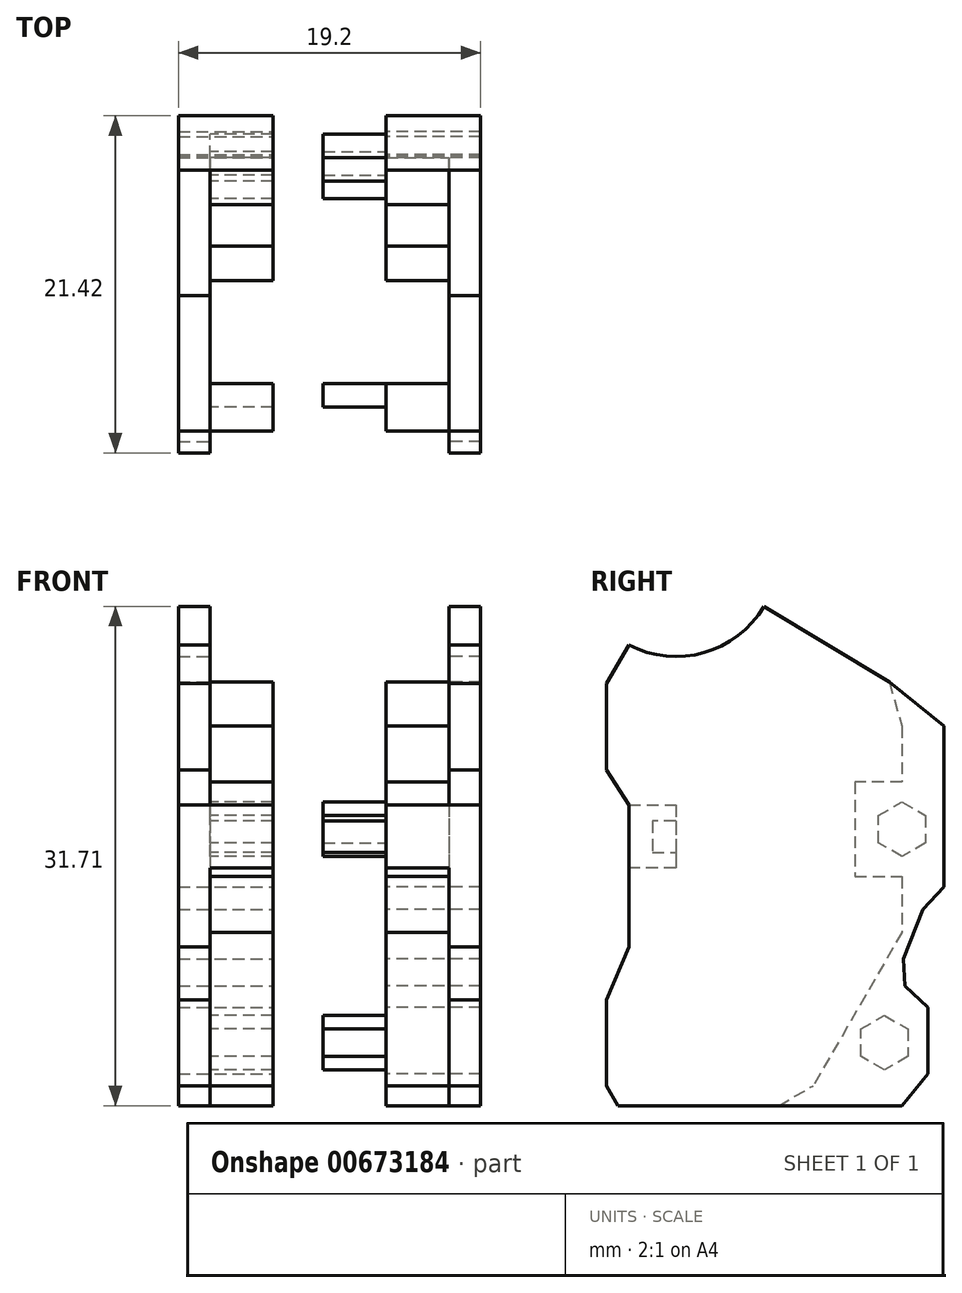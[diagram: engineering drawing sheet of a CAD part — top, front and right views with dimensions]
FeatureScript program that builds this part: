
annotation { "Feature Type Name" : "Feature", "Feature Type Description" : "" }
export const myFeature = defineFeature(function(context is Context, id is Id, definition is map)
    precondition{}
    {
        {
            var Q0;
            Q0=qCreatedBy(makeId("Right.planeOp"),FACE);
            cPlane(context, id + "F0", {"entities" : qUnion([Q0]), "cplaneType" : CPlaneType.OFFSET, "offset" : 7.6 * mm, "width" : 150 * mm, "height" : 150 * mm});
        }
        {
            var Q0;
            Q0=qCreatedBy(makeId("Right.planeOp"),FACE);
            var sketch = newSketch(context, id + "F1", { "sketchPlane" : qUnion([Q0])});
            skLineSegment(sketch, "E0.4", {"start": v(1.48, 13.79) * mm, "end": v(1.48, 12.29) * mm, "construction": true});
            skLineSegment(sketch, "E0.12", {"start": v(1.48, 9.69) * mm, "end": v(1.48, 2.79) * mm, "construction": true});
            skLineSegment(sketch, "E1.MirrorCS", {"start": v(-0.77, 10.55) * mm, "end": v(-0.77, 9.69) * mm, "construction": true});
            skLineSegment(sketch, "E2.MirrorCS", {"start": v(-0.02, 10.99) * mm, "end": v(-0.77, 10.55) * mm, "construction": true});
            skLineSegment(sketch, "E3.MirrorCS", {"start": v(-0.02, 12.29) * mm, "end": v(-0.02, 10.99) * mm, "construction": true});
            skLineSegment(sketch, "E4.MirrorCS", {"start": v(1.48, 12.29) * mm, "end": v(-0.02, 12.29) * mm, "construction": true});
            skArc(sketch, "E5.MirrorCS", {"start": v(0.48, 14.79) * mm, "mid": v(1.18, 14.5) * mm, "end": v(1.48, 13.79) * mm, "construction": true});
            skLineSegment(sketch, "E6.MirrorCS", {"start": v(-6.02, 8.55) * mm, "end": v(-6.02, 9.69) * mm, "construction": true});
            skLineSegment(sketch, "E7.MirrorCS", {"start": v(-4.52, 12.29) * mm, "end": v(-6.02, 12.29) * mm, "construction": true});
            skLineSegment(sketch, "E8.MirrorCS", {"start": v(-4.52, 10.99) * mm, "end": v(-4.52, 12.29) * mm, "construction": true});
            skLineSegment(sketch, "E9.MirrorCS", {"start": v(-3.77, 9.69) * mm, "end": v(-3.77, 10.55) * mm, "construction": true});
            skLineSegment(sketch, "E10.MirrorCS", {"start": v(-3.77, 10.55) * mm, "end": v(-4.52, 10.99) * mm, "construction": true});
            skLineSegment(sketch, "E11.MirrorCS", {"start": v(-0.77, 9.69) * mm, "end": v(1.48, 9.69) * mm, "construction": true});
            skLineSegment(sketch, "E12.MirrorCS", {"start": v(-5.02, 14.79) * mm, "end": v(0.48, 14.79) * mm, "construction": true});
            skArc(sketch, "E13.MirrorCS", {"start": v(-6.02, 13.79) * mm, "mid": v(-5.73, 14.5) * mm, "end": v(-5.02, 14.79) * mm, "construction": true});
            skLineSegment(sketch, "E14.MirrorCS", {"start": v(-5.02, 6.82) * mm, "end": v(-6.02, 8.55) * mm, "construction": true});
            skArc(sketch, "E15.MirrorCS", {"start": v(1.48, 2.79) * mm, "mid": v(-5.4, -1.04) * mm, "end": v(-5.02, 6.82) * mm, "construction": true});
            skLineSegment(sketch, "E16.MirrorCS", {"start": v(-6.02, 12.29) * mm, "end": v(-6.02, 13.79) * mm, "construction": true});
            skLineSegment(sketch, "E17.MirrorCS", {"start": v(-6.02, 9.69) * mm, "end": v(-3.77, 9.69) * mm, "construction": true});
            skLineSegment(sketch, "E18", {"start": v(-6.02, 8.55) * mm, "end": v(-7.43, 10.99) * mm, "construction": true});
            skLineSegment(sketch, "E19", {"start": v(-7.43, 10.99) * mm, "end": v(-11.18, 10.99) * mm, "construction": true});
            skLineSegment(sketch, "E20", {"start": v(-7.43, 10.99) * mm, "end": v(-10.15, 12.25) * mm, "construction": true});
            skLineSegment(sketch, "E21", {"start": v(-10.15, 12.25) * mm, "end": v(-10.15, 16.25) * mm, "construction": true});
            skLineSegment(sketch, "E22", {"start": v(-10.15, 14.25) * mm, "end": v(-8.02, 14.25) * mm, "construction": true});
            skLineSegment(sketch, "E23", {"start": v(-10.15, 16.25) * mm, "end": v(-7.15, 21.25) * mm, "construction": true});
            skLineSegment(sketch, "E24", {"start": v(-7.15, 21.25) * mm, "end": v(4.13, 21.25) * mm, "construction": true});
            skLineSegment(sketch, "E25", {"start": v(4.13, 21.25) * mm, "end": v(7.28, 16.25) * mm, "construction": true});
            skLineSegment(sketch, "E26", {"start": v(7.28, 16.25) * mm, "end": v(7.28, 9.57) * mm, "construction": true});
            skLineSegment(sketch, "E27", {"start": v(7.28, 9.57) * mm, "end": v(1.48, 6.24) * mm, "construction": true});
            skLineSegment(sketch, "E28", {"start": v(1.48, 6.24) * mm, "end": v(1.48, 9.69) * mm, "construction": true});
            skArc(sketch, "E29", {"start": v(0.22, 5.9) * mm, "mid": v(-2.25, 7.22) * mm, "end": v(-5.02, 6.82) * mm, "construction": true});
            skLineSegment(sketch, "E30", {"start": v(1.48, 6.24) * mm, "end": v(0.22, 5.9) * mm, "construction": true});
            skCircle(sketch, "E31", {"center": v(-3.02, 2.79) * mm, "radius": 4.5 * mm});
            skCircle(sketch, "E32", {"center": v(-3.02, 2.79) * mm, "radius": 3.5 * mm});
            skLineSegment(sketch, "E33", {"start": v(-3.02, 2.79) * mm, "end": v(-7.52, 2.79) * mm, "construction": true});
            skPoint(sketch, "E34.MirrorCS.end.orphan", {"position": v(-7.43, -5.42) * mm});
            skPoint(sketch, "E34.MirrorCS.start.orphan", {"position": v(-6.02, -2.98) * mm});
            skPoint(sketch, "E35.MirrorCS.start.orphan", {"position": v(-5.02, -1.25) * mm});
            skLineSegment(sketch, "E36", {"start": v(-5.02, -1.25) * mm, "end": v(-7.43, -5.42) * mm});
            skLineSegment(sketch, "E37", {"start": v(-6.02, -2.98) * mm, "end": v(-6.02, -30.98) * mm, "construction": true});
            skLineSegment(sketch, "E38", {"start": v(-7.43, -5.42) * mm, "end": v(-7.43, -10.9) * mm});
            skLineSegment(sketch, "E39", {"start": v(-7.43, -10.9) * mm, "end": v(-6.02, -13.15) * mm});
            skLineSegment(sketch, "E40", {"start": v(-6.02, -13.15) * mm, "end": v(-6.02, -22.15) * mm});
            skLineSegment(sketch, "E41", {"start": v(-6.02, -22.15) * mm, "end": v(-7.43, -25.53) * mm});
            skLineSegment(sketch, "E42", {"start": v(-7.43, -25.53) * mm, "end": v(-7.43, -30.98) * mm});
            skLineSegment(sketch, "E43", {"start": v(-7.43, -30.98) * mm, "end": v(-6.02, -33.4) * mm});
            skLineSegment(sketch, "E44", {"start": v(-6.02, -33.4) * mm, "end": v(1.48, -33.4) * mm});
            skLineSegment(sketch, "E45", {"start": v(1.48, -33.4) * mm, "end": v(1.48, 2.79) * mm, "construction": true});
            skLineSegment(sketch, "E46", {"start": v(1.48, -33.4) * mm, "end": v(5.7, -30.98) * mm});
            skLineSegment(sketch, "E47", {"start": v(1.48, 0.12) * mm, "end": v(1.48, 2.79) * mm});
            skLineSegment(sketch, "E48", {"start": v(10.53, -5.34) * mm, "end": v(11.33, -8.13) * mm});
            skLineSegment(sketch, "E49", {"start": v(11.33, -8.13) * mm, "end": v(11.33, -11.68) * mm});
            skLineSegment(sketch, "E50", {"start": v(11.33, -21.24) * mm, "end": v(5.7, -30.98) * mm});
            skPoint(sketch, "E51.end.orphan", {"position": v(7.28, -24.1) * mm});
            skPoint(sketch, "E52.orphan", {"position": v(9.73, -2.54) * mm});
            skPoint(sketch, "E53.orphan", {"position": v(1.48, -2.54) * mm});
            skPoint(sketch, "E54.start.orphan", {"position": v(5.6, -2.54) * mm});
            skLineSegment(sketch, "E55", {"start": v(1.48, 0.12) * mm, "end": v(1.91, -0.14) * mm});
            skLineSegment(sketch, "E56", {"start": v(11.33, -11.68) * mm, "end": v(8.33, -11.68) * mm});
            skLineSegment(sketch, "E57", {"start": v(8.33, -11.68) * mm, "end": v(8.33, -17.68) * mm});
            skLineSegment(sketch, "E58", {"start": v(8.33, -17.68) * mm, "end": v(11.33, -17.68) * mm});
            skLineSegment(sketch, "E59.trimOffspring", {"start": v(11.33, -17.68) * mm, "end": v(11.33, -21.24) * mm});
            skPoint(sketch, "E60.start.orphan", {"position": v(11.33, -14.68) * mm});
            skLineSegment(sketch, "E61", {"start": v(1.91, -0.14) * mm, "end": v(2.86, 2.73) * mm});
            skLineSegment(sketch, "E62", {"start": v(2.86, 2.73) * mm, "end": v(2.86, 5.9) * mm});
            skLineSegment(sketch, "E63", {"start": v(2.86, 5.9) * mm, "end": v(8.23, 9.33) * mm});
            skLineSegment(sketch, "E64", {"start": v(8.23, 9.33) * mm, "end": v(8.71, 10.78) * mm});
            skLineSegment(sketch, "E65", {"start": v(8.71, 10.78) * mm, "end": v(10.24, 10.27) * mm});
            skLineSegment(sketch, "E66", {"start": v(10.24, 10.27) * mm, "end": v(12.91, 5.96) * mm});
            skLineSegment(sketch, "E67", {"start": v(12.91, 5.96) * mm, "end": v(12.91, 0.6) * mm});
            skLineSegment(sketch, "E68", {"start": v(12.91, 0.6) * mm, "end": v(10.53, -5.34) * mm});
            skLineSegment(sketch, "E69", {"start": v(10.53, -5.34) * mm, "end": v(1.91, -0.14) * mm});
            skArc(sketch, "E70", {"start": v(-6.02, -2.98) * mm, "mid": v(-1.25, -3.46) * mm, "end": v(2.56, -0.53) * mm});
            skLineSegment(sketch, "E71", {"start": v(10.53, -5.34) * mm, "end": v(14, -8.13) * mm});
            skLineSegment(sketch, "E72", {"start": v(14, -8.13) * mm, "end": v(14, -18.34) * mm});
            skLineSegment(sketch, "E73", {"start": v(14, -18.34) * mm, "end": v(12.66, -19.79) * mm});
            skCircle(sketch, "E74.cCircle", {"center": v(11.33, -14.68) * mm, "radius": 1.5 * mm, "construction": true});
            skLineSegment(sketch, "E74.0", {"start": v(9.83, -15.55) * mm, "end": v(9.83, -13.82) * mm});
            skLineSegment(sketch, "E74.1", {"start": v(9.83, -13.82) * mm, "end": v(11.33, -12.95) * mm});
            skLineSegment(sketch, "E74.2", {"start": v(11.33, -12.95) * mm, "end": v(12.83, -13.82) * mm});
            skLineSegment(sketch, "E74.3", {"start": v(12.83, -13.82) * mm, "end": v(12.83, -15.55) * mm});
            skLineSegment(sketch, "E74.4", {"start": v(12.83, -15.55) * mm, "end": v(11.33, -16.41) * mm});
            skLineSegment(sketch, "E74.5", {"start": v(11.33, -16.41) * mm, "end": v(9.83, -15.55) * mm});
            skPoint(sketch, "E74.0.midPoint", {"position": v(9.83, -14.68) * mm});
            skLineSegment(sketch, "E75", {"start": v(-6.02, -13.15) * mm, "end": v(-3.02, -13.15) * mm});
            skLineSegment(sketch, "E76", {"start": v(-3.02, -13.15) * mm, "end": v(-3.02, -17.15) * mm});
            skLineSegment(sketch, "E77", {"start": v(-3.02, -17.15) * mm, "end": v(-6.02, -17.15) * mm});
            skLineSegment(sketch, "E78", {"start": v(-2.5, -15.15) * mm, "end": v(-2.5, -14.15) * mm, "construction": true});
            skPoint(sketch, "E78.startSnap0", {"position": v(-3.02, -15.15) * mm});
            skLineSegment(sketch, "E79", {"start": v(-3.02, -14.15) * mm, "end": v(-4.52, -14.15) * mm});
            skLineSegment(sketch, "E80", {"start": v(-4.52, -14.15) * mm, "end": v(-4.52, -16.15) * mm});
            skLineSegment(sketch, "E81", {"start": v(-4.52, -16.15) * mm, "end": v(-3.02, -16.15) * mm});
            skLineSegment(sketch, "E82", {"start": v(11.42, -22.93) * mm, "end": v(11.51, -24.63) * mm});
            skLineSegment(sketch, "E83", {"start": v(11.51, -24.63) * mm, "end": v(12.98, -26.01) * mm});
            skLineSegment(sketch, "E84", {"start": v(12.98, -26.01) * mm, "end": v(12.98, -30.21) * mm});
            skLineSegment(sketch, "E85", {"start": v(12.98, -30.21) * mm, "end": v(11.33, -32.24) * mm});
            skLineSegment(sketch, "E86", {"start": v(11.33, -32.24) * mm, "end": v(-6.7, -32.24) * mm});
            skLineSegment(sketch, "E87", {"start": v(12.66, -19.79) * mm, "end": v(11.42, -22.93) * mm});
            skCircle(sketch, "E88.cCircle", {"center": v(10.2, -28.24) * mm, "radius": 1.5 * mm, "construction": true});
            skLineSegment(sketch, "E88.0", {"start": v(8.7, -29.1) * mm, "end": v(8.7, -27.37) * mm});
            skLineSegment(sketch, "E88.1", {"start": v(8.7, -27.37) * mm, "end": v(10.2, -26.5) * mm});
            skLineSegment(sketch, "E88.2", {"start": v(10.2, -26.5) * mm, "end": v(11.7, -27.37) * mm});
            skLineSegment(sketch, "E88.3", {"start": v(11.7, -27.37) * mm, "end": v(11.7, -29.1) * mm});
            skLineSegment(sketch, "E88.4", {"start": v(11.7, -29.1) * mm, "end": v(10.2, -29.97) * mm});
            skLineSegment(sketch, "E88.5", {"start": v(10.2, -29.97) * mm, "end": v(8.7, -29.1) * mm});
            skPoint(sketch, "E88.0.midPoint", {"position": v(8.7, -28.24) * mm});
            skSolve(sketch);
        }
        {
            var Q0;
            {var subQ1=sQuery(id+"F1.wireOp",EDGE,"E38");Q0=makeQuery(id+"F1.imprint","IMPRINT",FACE,{"disambiguationData":[TD([[makeQuery(id+"F1.imprint","IMPRINT",EDGE,{"derivedFrom":subQ1}),1.0]])]});}
            var Q1;
            Q1=makeQuery(id+"F1.imprint","IMPRINT",FACE,{"disambiguationData":[TD([[makeQuery(id+"F1.imprint","IMPRINT",EDGE,{"derivedFrom":sQuery(id+"F1.wireOp",EDGE,"E48")}),1.0]])]});
            var Q2;
            Q2=makeQuery(id+"F1.imprint","IMPRINT",FACE,{"disambiguationData":[TD([[makeQuery(id+"F1.imprint","IMPRINT",EDGE,{"derivedFrom":sQuery(id+"F1.wireOp",EDGE,"E74.0")}),-1.0]])]});
            var Q3;
            {var subQ0=sQuery(id+"F1.wireOp",EDGE,"E75");Q3=makeQuery(id+"F1.imprint","IMPRINT",FACE,{"disambiguationData":[TD([[makeQuery(id+"F1.imprint","IMPRINT",EDGE,{"derivedFrom":subQ0}),-1.0]])]});}
            var Q4;
            {var subQ0=sQuery(id+"F1.wireOp",EDGE,"E79");Q4=makeQuery(id+"F1.imprint","IMPRINT",FACE,{"disambiguationData":[TD([[makeQuery(id+"F1.imprint","IMPRINT",EDGE,{"derivedFrom":subQ0}),1.0]])]});}
            var Q5;
            {var subQ0=sQuery(id+"F1.wireOp",EDGE,"E50");Q5=makeQuery(id+"F1.imprint","IMPRINT",FACE,{"disambiguationData":[TD([[makeQuery(id+"F1.imprint","IMPRINT",EDGE,{"derivedFrom":subQ0}),1.0]])]});}
            var Q6;
            Q6=makeQuery(id+"F1.imprint","IMPRINT",FACE,{"disambiguationData":[TD([[makeQuery(id+"F1.imprint","IMPRINT",EDGE,{"derivedFrom":sQuery(id+"F1.wireOp",EDGE,"E88.0")}),-1.0]])]});
            extrude(context, id + "F2", {"entities" : qUnion([Q0, Q1, Q2, Q3, Q4, Q5, Q6]), "oppositeDirection" : true, "depth" : 2 * mm});
        }
        {
            var Q0;
            Q0=makeQuery(id+"F1.imprint","IMPRINT",FACE,{"disambiguationData":[TD([[makeQuery(id+"F1.imprint","IMPRINT",EDGE,{"derivedFrom":sQuery(id+"F1.wireOp",EDGE,"E48")}),1.0]])]});
            var Q1;
            {var subQ0=sQuery(id+"F1.wireOp",EDGE,"E75");Q1=makeQuery(id+"F1.imprint","IMPRINT",FACE,{"disambiguationData":[TD([[makeQuery(id+"F1.imprint","IMPRINT",EDGE,{"derivedFrom":subQ0}),-1.0]])]});}
            var Q2;
            {var subQ0=sQuery(id+"F1.wireOp",EDGE,"E50");Q2=makeQuery(id+"F1.imprint","IMPRINT",FACE,{"disambiguationData":[TD([[makeQuery(id+"F1.imprint","IMPRINT",EDGE,{"derivedFrom":subQ0}),1.0]])]});}
            extrude(context, id + "F3", {"entities" : qUnion([Q0, Q1, Q2]), "operationType" : NewBodyOperationType.ADD, "depth" : 4 * mm});
        }
        {
            var Q0;
            Q0=makeQuery(id+"F2.opExtrude","SWEPT_BODY",BODY,{"disambiguationData":[OSD([sQuery(id+"F1.wireOp",EDGE,"E36"),sQuery(id+"F1.wireOp",EDGE,"E38"),sQuery(id+"F1.wireOp",EDGE,"E39"),sQuery(id+"F1.wireOp",EDGE,"E40"),sQuery(id+"F1.wireOp",EDGE,"E69"),sQuery(id+"F1.wireOp",EDGE,"E70"),sQuery(id+"F1.wireOp",EDGE,"u80SHiFu-pKp3-5241-QGfv-MUt3mfUZoovk"),sQuery(id+"F1.wireOp",EDGE,"E71"),sQuery(id+"F1.wireOp",EDGE,"E72"),sQuery(id+"F1.wireOp",EDGE,"E73")])]});
            var Q1;
            Q1=qCreatedBy(id+"F0.planeOp",FACE);
            mirror(context, id + "F4", {"entities" : qUnion([Q0]), "mirrorPlane" : qUnion([Q1])});
        }
        {
            var Q0;
            Q0=makeQuery(id+"F4.opPattern","COPY",FACE,{"derivedFrom":makeQuery(id+"F3.boolean.opBoolean","SPLIT",FACE,{"disambiguationData":[TD([makeQuery(id+"F3.opExtrude","SWEPT_FACE",FACE,{"disambiguationData":[OSD([sQuery(id+"F1.wireOp",EDGE,"E74.0")])]})])],"derivedFrom":makeQuery(id+"F2.opExtrude","CAP_FACE",FACE,{"disambiguationData":[OSD([sQuery(id+"F1.wireOp",EDGE,"E36"),sQuery(id+"F1.wireOp",EDGE,"E38"),sQuery(id+"F1.wireOp",EDGE,"E39"),sQuery(id+"F1.wireOp",EDGE,"E40"),sQuery(id+"F1.wireOp",EDGE,"E69"),sQuery(id+"F1.wireOp",EDGE,"E70"),sQuery(id+"F1.wireOp",EDGE,"u80SHiFu-pKp3-5241-QGfv-MUt3mfUZoovk"),sQuery(id+"F1.wireOp",EDGE,"E71"),sQuery(id+"F1.wireOp",EDGE,"E72"),sQuery(id+"F1.wireOp",EDGE,"E73")])],"isStart":true})}),"instanceName":"1"});
            extrude(context, id + "F5", {"entities" : qUnion([Q0]), "operationType" : NewBodyOperationType.ADD, "depth" : 8 * mm});
        }
        {
            var Q0;
            {var subQ0=sQuery(id+"F1.wireOp",EDGE,"E73");var subQ1=sQuery(id+"F1.wireOp",EDGE,"E71");var subQ2=sQuery(id+"F1.wireOp",EDGE,"E39");var subQ4=sQuery(id+"F1.wireOp",EDGE,"E38");var subQ5=sQuery(id+"F1.wireOp",EDGE,"E40");var subQ6=sQuery(id+"F1.wireOp",EDGE,"E36");var subQ10=sQuery(id+"F1.wireOp",EDGE,"E69");var subQ12=sQuery(id+"F1.wireOp",EDGE,"E70");var subQ13=sQuery(id+"F1.wireOp",EDGE,"u80SHiFu-pKp3-5241-QGfv-MUt3mfUZoovk");Q0=makeQuery(id+"F4.opPattern","COPY",FACE,{"derivedFrom":makeQuery(id+"F3.boolean.opBoolean","SPLIT",FACE,{"disambiguationData":[TD([makeQuery(id+"F2.opExtrude","SWEPT_FACE",FACE,{"disambiguationData":[OSD([subQ6])]})])],"derivedFrom":makeQuery(id+"F2.opExtrude","CAP_FACE",FACE,{"disambiguationData":[OSD([subQ6,subQ4,subQ2,subQ5,subQ10,subQ12,subQ13,subQ1,sQuery(id+"F1.wireOp",EDGE,"E72"),subQ0])],"isStart":true})}),"instanceName":"1"});}
            var sketch = newSketch(context, id + "F6", { "sketchPlane" : qUnion([Q0])});
            skLineSegment(sketch, "E89", {"start": v(3.02, -14.15) * mm, "end": v(3.02, -16.15) * mm});
            skSolve(sketch);
        }
        {
            var Q0;
            Q0=qSketchRegion(id+"F6",true);
            var Q1;
            Q1=makeQuery(id+"F6.imprint","IMPRINT",FACE,{"disambiguationData":[TD([[makeQuery(id+"F6.imprint","IMPRINT",EDGE,{"derivedFrom":sQuery(id+"F6.wireOp",EDGE,"E89")}),1.0]])]});
            var Q2;
            Q2=makeQuery(id+"F4.opPattern","COPY",FACE,{"derivedFrom":makeQuery(id+"F3.boolean.opBoolean","SPLIT",FACE,{"disambiguationData":[TD([makeQuery(id+"F3.opExtrude","SWEPT_FACE",FACE,{"disambiguationData":[OSD([sQuery(id+"F1.wireOp",EDGE,"E88.0")])]})])],"derivedFrom":makeQuery(id+"F2.opExtrude","CAP_FACE",FACE,{"disambiguationData":[OSD([sQuery(id+"F1.wireOp",EDGE,"E36"),sQuery(id+"F1.wireOp",EDGE,"E38"),sQuery(id+"F1.wireOp",EDGE,"E39"),sQuery(id+"F1.wireOp",EDGE,"E40"),sQuery(id+"F1.wireOp",EDGE,"E41"),sQuery(id+"F1.wireOp",EDGE,"E42"),sQuery(id+"F1.wireOp",EDGE,"E43"),sQuery(id+"F1.wireOp",EDGE,"E69"),sQuery(id+"F1.wireOp",EDGE,"E70"),sQuery(id+"F1.wireOp",EDGE,"E71"),sQuery(id+"F1.wireOp",EDGE,"E72"),sQuery(id+"F1.wireOp",EDGE,"E73"),sQuery(id+"F1.wireOp",EDGE,"E82"),sQuery(id+"F1.wireOp",EDGE,"E83"),sQuery(id+"F1.wireOp",EDGE,"E84"),sQuery(id+"F1.wireOp",EDGE,"E85"),sQuery(id+"F1.wireOp",EDGE,"E86"),sQuery(id+"F1.wireOp",EDGE,"E87")])],"isStart":true})}),"instanceName":"1"});
            extrude(context, id + "F7", {"entities" : qUnion([Q0, Q1, Q2]), "operationType" : NewBodyOperationType.ADD, "depth" : 8 * mm});
        }
    });
